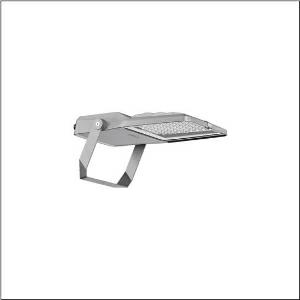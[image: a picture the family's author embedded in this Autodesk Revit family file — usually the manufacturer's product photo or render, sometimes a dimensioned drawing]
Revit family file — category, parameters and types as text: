
# Revit family: floodlight_fl_21_mini___pl61_5xa7772b4c1a_d176
name_source: partatom
category: Lighting Fixtures
units: mm (PartAtom-declared; Revit-internal decimal feet)

## family parameters
Cut with Voids When Loaded = No
Host = Face
Light Source = No
Part Type = Normal
Room Calculation Point = No
Round Connector Dimension = Use Diameter
Shared = No

## types (1)
- --- (1 x LED, 6370 lm, 45.5 W, 4000K)
    Apparent Load = 46 VA
    CIE Flux Codes = 33 65 98 100 100
    Color Rendering = 70
    Color Temperature = 4000K
    Default Elevation = 1800 mm
    Description = Floodlight FL 21 mini, floodlight, primary light control with lens, of PMMA, primary optical cover: protective disc, of toughened safety glass, transparent, light distribution: PL61, light emission: direct distribution, installation type: surface-mounted, LED, High Power LED, rated luminous flux: 6.370lm, luminous efficacy: 140lm/W, light colour: 740, colour temperature: 4000K, control gear: ECG iQ, control: Street-Remote, Auto-Match, Temp-Guard, Night-Set, Smart-Wire, Desk-Remote (wireless, voltage-free reading and setting of iQ features in the workshop via application-optimized NFC function/RFID function), optimised constant luminous flux control (CLO 2.0), with terminal, 6-pole, mains connection: 220..240V, AC, 50/60Hz, start of lifetime: 46W, end of lifetime: 48W, reduction: 22W, luminaire housing, of diecast aluminium, powder-coated, Siteco® metallic grey (DB 702S), corrosivity category C5 according to DIN EN ISO 12944, mounting bracket, of steel, galvanised, powder-coated, Siteco® metallic grey (DB 702S), protection rating (complete): IP66, insulation class (complete): insulation class II (safety insulation), certification: CE, ENEC, VDE, protection symbol: D, impact resistance: IK08, permissible operating ambient temperature: -40..+40°C, permissible operating ambient temperature for outdoor applications: -40..+50°C, standard: DIN EN 12944, packaging unit: 1 piece

Light Distribution: PL61
    Height = 70 mm
    Lamp = 1 x LED
    Lamp Light Flux = 6370 lm
    Lamp Power = 45.5 W
    Lamp count = 1
    Length = 485 mm
    Luminous efficacy = 140 lm/W
    Manufacturer = Siteco
    ModVariant = No
    Model = 5XA7772B4C1A
    Number of Poles = 1
    OnlyDefault = Yes
    Power Factor = 1
    Product Name = Floodlight FL 21 mini | PL61
    Product group = floodlight | pylon top
    ProductGroupID = 6101
    Protection Class = Protection class II
    Protection Degree = IP 66
    RLX_Detail_Level = 1
    RlxData = <blob elided: 96157 chars, md5=3d799705>
    Socket = socket
    Standby Power = 0 W
    System Light Flux = 6370 lm
    System Power = 46 W
    Type Comments = factory setting: luminous flux: 100 % | dim-lin: 254 | 463 mA
    Type Image = l_1006845.jpg
    URL = http://relux.com
    VarID = @adj_085837
    Voltage = 0 V
    Weight = 0.00 kg
    Width = 337 mm

## geometry (parser evidence)
native form markers: Blend x4, Sweep x14
no freeform markers — native parametric forms only
